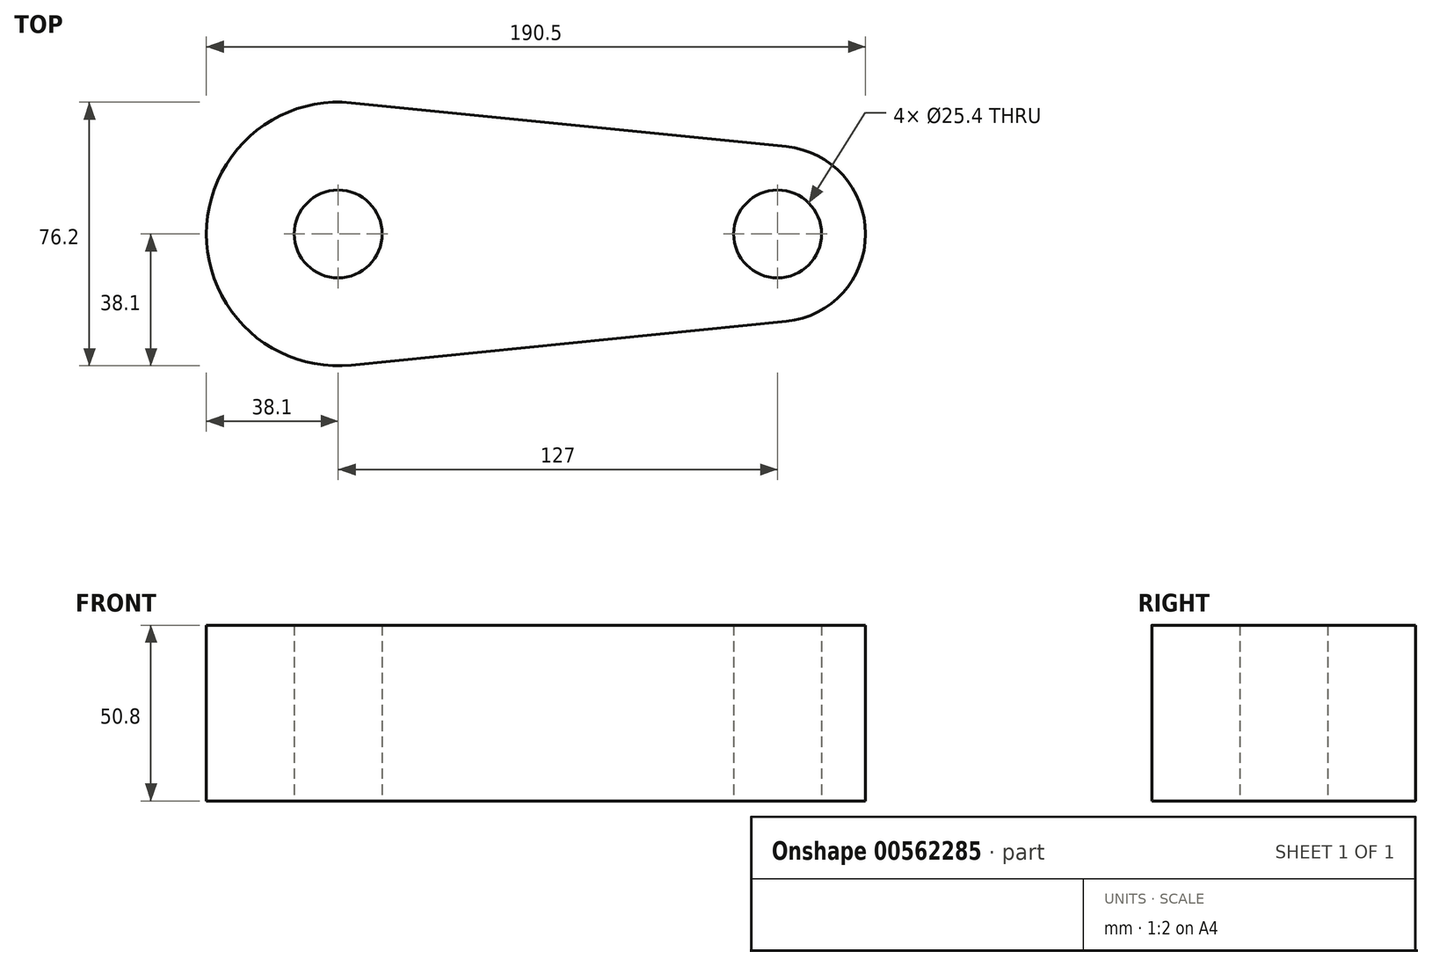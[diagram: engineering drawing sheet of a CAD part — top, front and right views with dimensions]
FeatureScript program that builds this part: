
annotation { "Feature Type Name" : "Feature", "Feature Type Description" : "" }
export const myFeature = defineFeature(function(context is Context, id is Id, definition is map)
    precondition{}
    {
        {
            var Q0;
            Q0=qCreatedBy(makeId("Top.planeOp"),FACE);
            var sketch = newSketch(context, id + "F0", { "sketchPlane" : qUnion([Q0])});
            skCircle(sketch, "E0", {"center": v(0, 0) * mm, "radius": 38.1 * mm});
            skCircle(sketch, "E1", {"center": v(127, 0) * mm, "radius": 25.4 * mm});
            skLineSegment(sketch, "E2", {"start": v(3.8, 37.9) * mm, "end": v(129.54, 25.27) * mm});
            skLineSegment(sketch, "E3", {"start": v(3.8, -37.9) * mm, "end": v(129.54, -25.27) * mm});
            skCircle(sketch, "E4", {"center": v(0, 0) * mm, "radius": 12.7 * mm});
            skCircle(sketch, "E5", {"center": v(127, 0) * mm, "radius": 12.7 * mm});
            skSolve(sketch);
        }
        {
            var Q0;
            Q0 = qSketchRegion(id + "F0", true);
            extrude(context, id + "F1", {"entities" : qUnion([Q0]), "depth" : 50.8 * mm, "offsetDistance" : 25.4 * mm});
        }
        {
            var Q0;
            Q0=sQuery(id+"F0.wireOp",EDGE,"E0");
            var Q1;
            Q1=sQuery(id+"F0.wireOp",EDGE,"E4");
            extrude(context, id + "F2", {"bodyType" : ToolBodyType.SURFACE, "surfaceEntities" : qUnion([Q0, Q1]), "depth" : 76.2 * mm, "offsetDistance" : 25.4 * mm});
        }
    });
